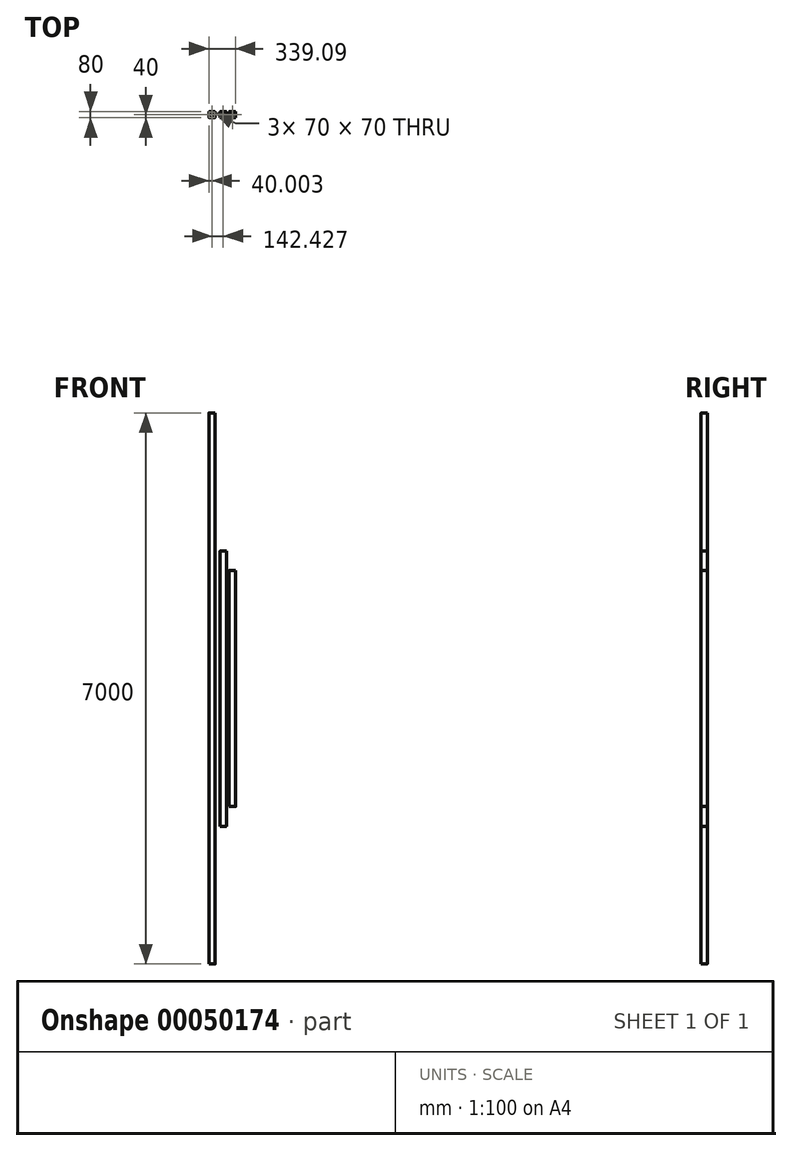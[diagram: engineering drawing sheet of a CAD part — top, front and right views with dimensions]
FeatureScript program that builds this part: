
annotation { "Feature Type Name" : "Feature", "Feature Type Description" : "" }
export const myFeature = defineFeature(function(context is Context, id is Id, definition is map)
    precondition{}
    {
        {
            var Q0;
            Q0=qCreatedBy(makeId("Top.planeOp"),FACE);
            var sketch = newSketch(context, id + "F0", { "sketchPlane" : qUnion([Q0])});
            skLineSegment(sketch, "E0.rect.bottom", {"start": v(40, 40) * mm, "end": v(-40, 40) * mm});
            skLineSegment(sketch, "E0.rect.top", {"start": v(40, -40) * mm, "end": v(-40, -40) * mm});
            skLineSegment(sketch, "E0.rect.left", {"start": v(40, 40) * mm, "end": v(40, -40) * mm});
            skLineSegment(sketch, "E0.rect.right", {"start": v(-40, 40) * mm, "end": v(-40, -40) * mm});
            skPoint(sketch, "E0.rect.middle", {"position": v(0, 0) * mm});
            skLineSegment(sketch, "E1.0", {"start": v(-35, 35) * mm, "end": v(-35, -35) * mm});
            skLineSegment(sketch, "E1.1", {"start": v(35, 35) * mm, "end": v(-35, 35) * mm});
            skLineSegment(sketch, "E1.2", {"start": v(35, 35) * mm, "end": v(35, -35) * mm});
            skLineSegment(sketch, "E1.3", {"start": v(35, -35) * mm, "end": v(-35, -35) * mm});
            skSolve(sketch);
        }
        {
            var Q0;
            Q0=makeQuery(id+"F0.imprint","IMPRINT",FACE,{"disambiguationData":[TD([[makeQuery(id+"F0.imprint","IMPRINT",EDGE,{"derivedFrom":sQuery(id+"F0.wireOp",EDGE,"E0.rect.bottom")}),1.0]])]});
            extrude(context, id + "F1", {"entities" : qUnion([Q0]), "depth" : 3500 * mm, "symmetric" : true});
        }
        {
            var Q0;
            Q0=qCreatedBy(makeId("Top.planeOp"),FACE);
            var sketch = newSketch(context, id + "F2", { "sketchPlane" : qUnion([Q0])});
            skLineSegment(sketch, "E2.rect.bottom", {"start": v(156.66, 40) * mm, "end": v(76.66, 40) * mm});
            skLineSegment(sketch, "E2.rect.top", {"start": v(156.66, -40) * mm, "end": v(76.66, -40) * mm});
            skLineSegment(sketch, "E2.rect.left", {"start": v(156.66, 40) * mm, "end": v(156.66, -40) * mm});
            skLineSegment(sketch, "E2.rect.right", {"start": v(76.66, 40) * mm, "end": v(76.66, -40) * mm});
            skPoint(sketch, "E2.rect.middle", {"position": v(116.66, 0) * mm});
            skLineSegment(sketch, "E3.0", {"start": v(81.66, 35) * mm, "end": v(81.66, -35) * mm});
            skLineSegment(sketch, "E3.1", {"start": v(151.66, 35) * mm, "end": v(81.66, 35) * mm});
            skLineSegment(sketch, "E3.2", {"start": v(151.66, 35) * mm, "end": v(151.66, -35) * mm});
            skLineSegment(sketch, "E3.3", {"start": v(151.66, -35) * mm, "end": v(81.66, -35) * mm});
            skSolve(sketch);
        }
        {
            var Q0;
            Q0=makeQuery(id+"F2.imprint","IMPRINT",FACE,{"disambiguationData":[TD([[makeQuery(id+"F2.imprint","IMPRINT",EDGE,{"derivedFrom":sQuery(id+"F2.wireOp",EDGE,"E2.rect.bottom")}),1.0]])]});
            extrude(context, id + "F3", {"entities" : qUnion([Q0]), "depth" : 3000 * mm, "symmetric" : true});
        }
        {
            var Q0;
            Q0=qCreatedBy(makeId("Top.planeOp"),FACE);
            var sketch = newSketch(context, id + "F4", { "sketchPlane" : qUnion([Q0])});
            skLineSegment(sketch, "E4.rect.bottom", {"start": v(-102.43, 40) * mm, "end": v(-182.43, 40) * mm});
            skLineSegment(sketch, "E4.rect.top", {"start": v(-102.43, -40) * mm, "end": v(-182.43, -40) * mm});
            skLineSegment(sketch, "E4.rect.left", {"start": v(-102.43, 40) * mm, "end": v(-102.43, -40) * mm});
            skLineSegment(sketch, "E4.rect.right", {"start": v(-182.43, 40) * mm, "end": v(-182.43, -40) * mm});
            skPoint(sketch, "E4.rect.middle", {"position": v(-142.43, 0) * mm});
            skLineSegment(sketch, "E5.0", {"start": v(-177.43, 35) * mm, "end": v(-177.43, -35) * mm});
            skLineSegment(sketch, "E5.1", {"start": v(-107.43, 35) * mm, "end": v(-177.43, 35) * mm});
            skLineSegment(sketch, "E5.2", {"start": v(-107.43, 35) * mm, "end": v(-107.43, -35) * mm});
            skLineSegment(sketch, "E5.3", {"start": v(-107.43, -35) * mm, "end": v(-177.43, -35) * mm});
            skSolve(sketch);
        }
        {
            var Q0;
            Q0=makeQuery(id+"F4.imprint","IMPRINT",FACE,{"disambiguationData":[TD([[makeQuery(id+"F4.imprint","IMPRINT",EDGE,{"derivedFrom":sQuery(id+"F4.wireOp",EDGE,"E4.rect.bottom")}),1.0]])]});
            extrude(context, id + "F5", {"entities" : qUnion([Q0]), "depth" : 7000 * mm, "symmetric" : true});
        }
        {
            var Q0;
            Q0=makeQuery(id+"F1.opExtrude","SWEPT_EDGE",EDGE,{"disambiguationData":[OSD([sQuery(id+"F0.wireOp",EDGE,"E0.rect.bottom"),sQuery(id+"F0.wireOp",EDGE,"E0.rect.right")])]});
            var Q1;
            Q1=makeQuery(id+"F1.opExtrude","SWEPT_EDGE",EDGE,{"disambiguationData":[OSD([sQuery(id+"F0.wireOp",EDGE,"E0.rect.top"),sQuery(id+"F0.wireOp",EDGE,"E0.rect.right")])]});
            var Q2;
            Q2=makeQuery(id+"F1.opExtrude","SWEPT_EDGE",EDGE,{"disambiguationData":[OSD([sQuery(id+"F0.wireOp",EDGE,"E0.rect.top"),sQuery(id+"F0.wireOp",EDGE,"E0.rect.left")])]});
            var Q3;
            Q3=makeQuery(id+"F1.opExtrude","SWEPT_EDGE",EDGE,{"disambiguationData":[OSD([sQuery(id+"F0.wireOp",EDGE,"E0.rect.bottom"),sQuery(id+"F0.wireOp",EDGE,"E0.rect.left")])]});
            var Q4;
            Q4=makeQuery(id+"F3.opExtrude","SWEPT_EDGE",EDGE,{"disambiguationData":[OSD([sQuery(id+"F2.wireOp",EDGE,"E2.rect.top"),sQuery(id+"F2.wireOp",EDGE,"E2.rect.left")])]});
            var Q5;
            Q5=makeQuery(id+"F3.opExtrude","SWEPT_EDGE",EDGE,{"disambiguationData":[OSD([sQuery(id+"F2.wireOp",EDGE,"E2.rect.top"),sQuery(id+"F2.wireOp",EDGE,"E2.rect.right")])]});
            var Q6;
            Q6=makeQuery(id+"F3.opExtrude","SWEPT_EDGE",EDGE,{"disambiguationData":[OSD([sQuery(id+"F2.wireOp",EDGE,"E2.rect.bottom"),sQuery(id+"F2.wireOp",EDGE,"E2.rect.left")])]});
            var Q7;
            Q7=makeQuery(id+"F3.opExtrude","SWEPT_EDGE",EDGE,{"disambiguationData":[OSD([sQuery(id+"F2.wireOp",EDGE,"E2.rect.bottom"),sQuery(id+"F2.wireOp",EDGE,"E2.rect.right")])]});
            var Q8;
            Q8=makeQuery(id+"F5.opExtrude","SWEPT_EDGE",EDGE,{"disambiguationData":[OSD([sQuery(id+"F4.wireOp",EDGE,"E4.rect.top"),sQuery(id+"F4.wireOp",EDGE,"E4.rect.left")])]});
            var Q9;
            Q9=makeQuery(id+"F5.opExtrude","SWEPT_EDGE",EDGE,{"disambiguationData":[OSD([sQuery(id+"F4.wireOp",EDGE,"E4.rect.top"),sQuery(id+"F4.wireOp",EDGE,"E4.rect.right")])]});
            var Q10;
            Q10=makeQuery(id+"F5.opExtrude","SWEPT_EDGE",EDGE,{"disambiguationData":[OSD([sQuery(id+"F4.wireOp",EDGE,"E4.rect.bottom"),sQuery(id+"F4.wireOp",EDGE,"E4.rect.left")])]});
            var Q11;
            Q11=makeQuery(id+"F5.opExtrude","SWEPT_EDGE",EDGE,{"disambiguationData":[OSD([sQuery(id+"F4.wireOp",EDGE,"E4.rect.bottom"),sQuery(id+"F4.wireOp",EDGE,"E4.rect.right")])]});
            fillet(context, id + "F6", {"entities" : qUnion([Q0, Q1, Q2, Q3, Q4, Q5, Q6, Q7, Q8, Q9, Q10, Q11]), "radius" : 5 * mm, "tangentPropagation" : true, "allowEdgeOverflow" : false});
        }
    });
